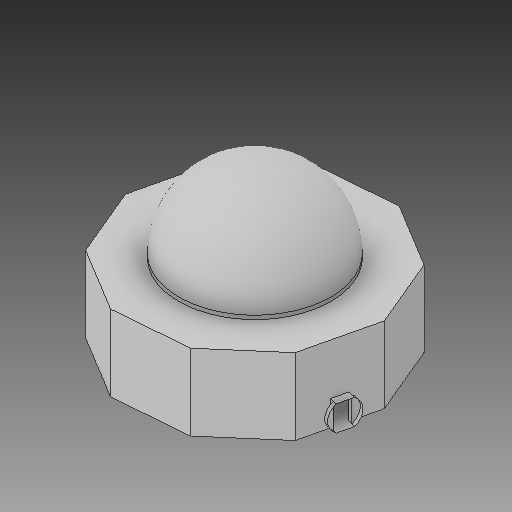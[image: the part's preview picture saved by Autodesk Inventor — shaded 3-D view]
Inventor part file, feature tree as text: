
AUTODESK INVENTOR PART (.ipt)
format: ipt  version: 2017 (Build 210142000, 142)  size: 227,328 bytes
history: native  units: in
note: dims shown in document units (in); Inventor stores cm internally (conversion verified against a paired STEP export)
features: extrude x5, sketch x5, other x2, delete_face x1
ambient origin geometry x8: Origin, YZ Plane, XZ Plane, XY Plane, X Axis, Y Axis, Z Axis, Center Point
bodies: Solid1 (feature_tree)
feature tree (13):
  extrude  "bace"  Depth=1.0in TaperAngle=0.0deg
  extrude  "bace wall"  Depth=20.0in TaperAngle=0.0deg
  extrude  "bace ceiling"  Depth=6.6667in
  other  "dome work plane"
  other  "dome"
  extrude  "door frame"  Depth=1.0in
  extrude  "corridor connection"  Depth=21.0in
  delete_face  "Delete Face6"
  sketch  "Sketch1"  dims[d0=62.0in d1=1.0in d2=0.0in]
  sketch  "Sketch2"  dims[d4=1.0in d5=20.0in d6=0.0in]
  sketch  "Sketch3"  dims[d8=1.0in d9=0.0in d16=2.0in d17=6.6667in]
  sketch  "Sketch8"  dims[d18=1.0in d19=0.0in d28=40.0in]
  sketch  "Sketch10"  dims[d32=20.0in d33=21.0in d34=90.0deg d91=4.0in d93=3.8873in d94=3.8873in d98=1.6458in d103=3.3333in d104=1.0in d106=1.0in d107=1.0in d108=0.0in]
